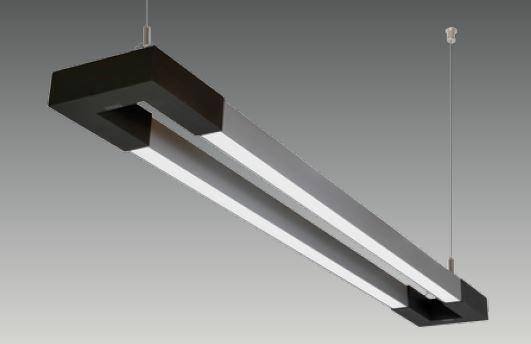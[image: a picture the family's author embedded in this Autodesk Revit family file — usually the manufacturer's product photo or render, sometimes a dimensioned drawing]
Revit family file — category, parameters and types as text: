
# Revit family: S 1500 RNG
name_source: partatom
category: Lighting Fixtures
revit_build: Autodesk Revit 2017 (Build: 20160225_1515(x64)
units: mm (PartAtom-declared; Revit-internal decimal feet)

## family parameters
Cut with Voids When Loaded = No
Host = Face
Light Source = Yes
Part Type = Normal
Room Calculation Point = No
Round Connector Dimension = Use Diameter
Shared = No

## types (2) — shared parameters
Color Filter = 16777215
Default Elevation = 1219 mm
Dimming Lamp Color Temperature Shift = <None>
Emit Shape Visible in Rendering = Yes
Emit from Rectangle Length = 1130 mm  [stored 3.70735 ft]
Emit from Rectangle Width = 40 mm  [stored 0.131234 ft]
Light Source Symbol Size = 610 mm
Manufacturer = ARLIGHT
Type Image = S 1500 RNG.JPG
Wattage Comments = 92W

## per-type parameters (varying)
| type | Apparent Load |
| SRNG.1500.92.30 | 92 VA |
| SRNG.1500.92.40 | 0 VA |

note: [stored X ft] marks values corroborated as IEEE doubles in the binary element streams (Revit-internal decimal feet)

## geometry (parser evidence)
native form markers: Sweep x5
no freeform markers — native parametric forms only
